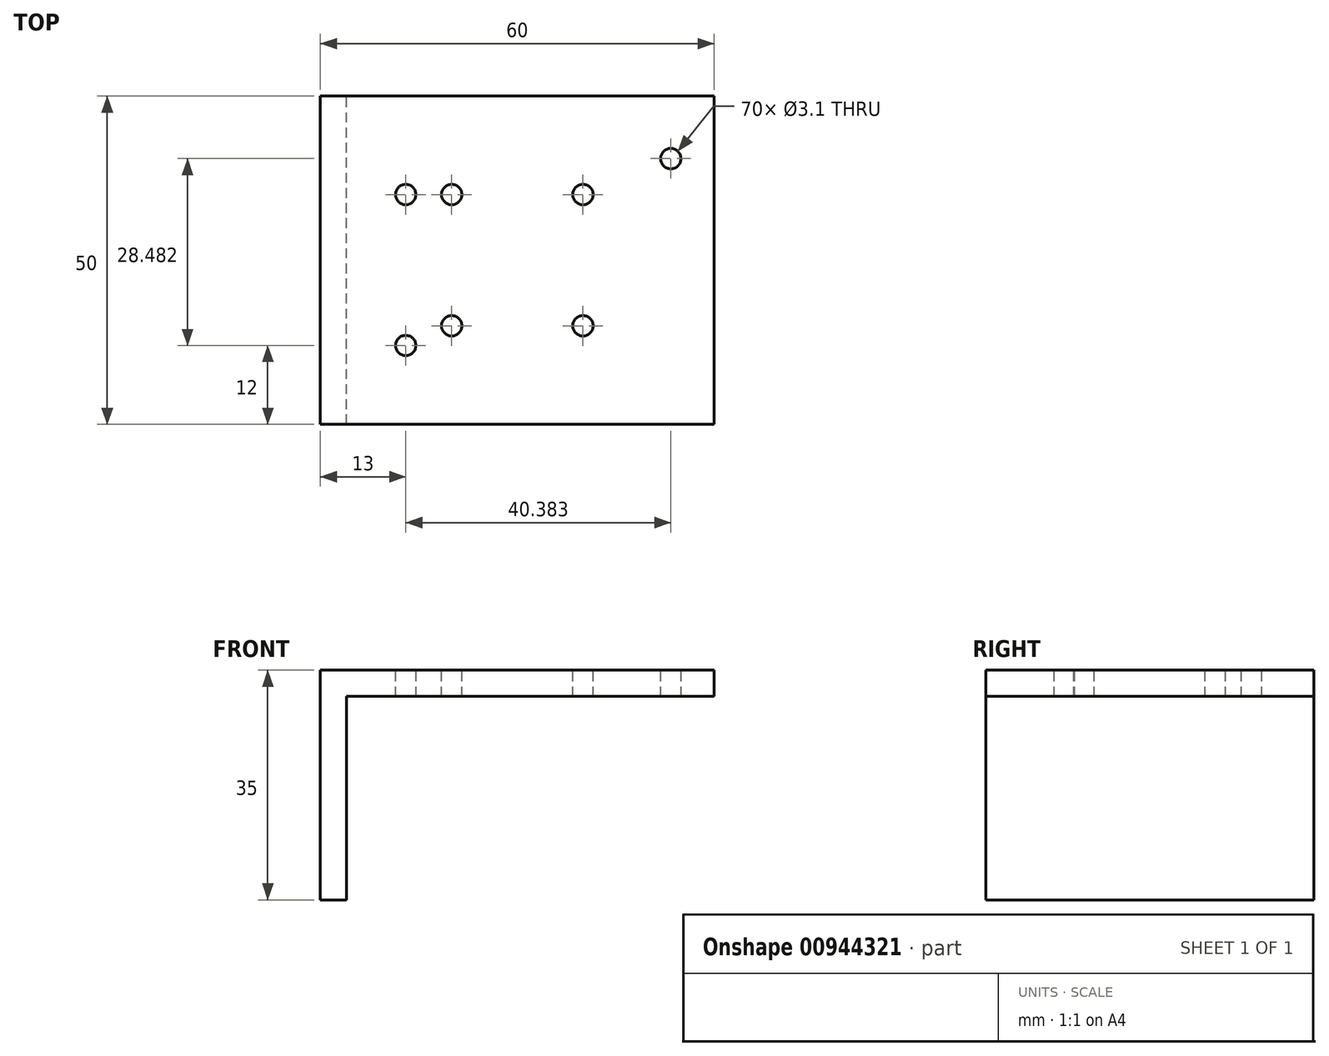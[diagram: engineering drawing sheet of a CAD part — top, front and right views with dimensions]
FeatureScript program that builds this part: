
annotation { "Feature Type Name" : "Feature", "Feature Type Description" : "" }
export const myFeature = defineFeature(function(context is Context, id is Id, definition is map)
    precondition{}
    {
        {
            var Q0;
            Q0=qCreatedBy(makeId("Front.planeOp"),FACE);
            var sketch = newSketch(context, id + "F0", { "sketchPlane" : qUnion([Q0])});
            skLineSegment(sketch, "E0", {"start": v(0, 0) * mm, "end": v(0, -35) * mm});
            skLineSegment(sketch, "E1", {"start": v(0, -35) * mm, "end": v(4, -35) * mm});
            skLineSegment(sketch, "E2", {"start": v(4, -35) * mm, "end": v(4, -4) * mm});
            skLineSegment(sketch, "E3", {"start": v(4, -4) * mm, "end": v(60, -4) * mm});
            skLineSegment(sketch, "E4", {"start": v(60, -4) * mm, "end": v(60, 0) * mm});
            skLineSegment(sketch, "E5", {"start": v(60, 0) * mm, "end": v(0, 0) * mm});
            skSolve(sketch);
        }
        {
            var Q0;
            Q0=makeQuery(id+"F0.imprint","IMPRINT",FACE,{"disambiguationData":[TD([[makeQuery(id+"F0.imprint","IMPRINT",EDGE,{"derivedFrom":sQuery(id+"F0.wireOp",EDGE,"E0")}),1.0]])]});
            extrude(context, id + "F1", {"entities" : qUnion([Q0]), "depth" : 50 * mm, "offsetDistance" : 25 * mm});
        }
        {
            var Q0;
            Q0=makeQuery(id+"F1.opExtrude","SWEPT_FACE",FACE,{"disambiguationData":[OSD([sQuery(id+"F0.wireOp",EDGE,"E5")])]});
            var sketch = newSketch(context, id + "F2", { "sketchPlane" : qUnion([Q0])});
            skLineSegment(sketch, "E6", {"start": v(0, -25) * mm, "end": v(60, -25) * mm, "construction": true});
            skLineSegment(sketch, "E7", {"start": v(30, 0) * mm, "end": v(30, -50) * mm, "construction": true});
            skCircle(sketch, "E8", {"center": v(40, -15) * mm, "radius": 1.55 * mm});
            skCircle(sketch, "E9.MirrorC", {"center": v(20, -15) * mm, "radius": 1.55 * mm});
            skCircle(sketch, "E10.MirrorC", {"center": v(20, -35) * mm, "radius": 1.55 * mm});
            skCircle(sketch, "E11.MirrorC", {"center": v(40, -35) * mm, "radius": 1.55 * mm});
            skLineSegment(sketch, "E12", {"start": v(13, -50) * mm, "end": v(13, 0) * mm, "construction": true});
            skCircle(sketch, "E13", {"center": v(13, -38) * mm, "radius": 1.55 * mm});
            skCircle(sketch, "E14", {"center": v(13, -15) * mm, "radius": 1.55 * mm});
            skCircle(sketch, "E15", {"center": v(53.38, -9.52) * mm, "radius": 1.55 * mm});
            skSolve(sketch);
        }
        {
            var Q0;
            Q0=qSketchRegion(id+"F2",true);
            extrude(context, id + "F3", {"entities" : qUnion([Q0]), "operationType" : NewBodyOperationType.REMOVE, "endBound" : BoundingType.UP_TO_NEXT, "oppositeDirection" : true, "depth" : 25 * mm, "offsetDistance" : 25 * mm});
        }
    });
